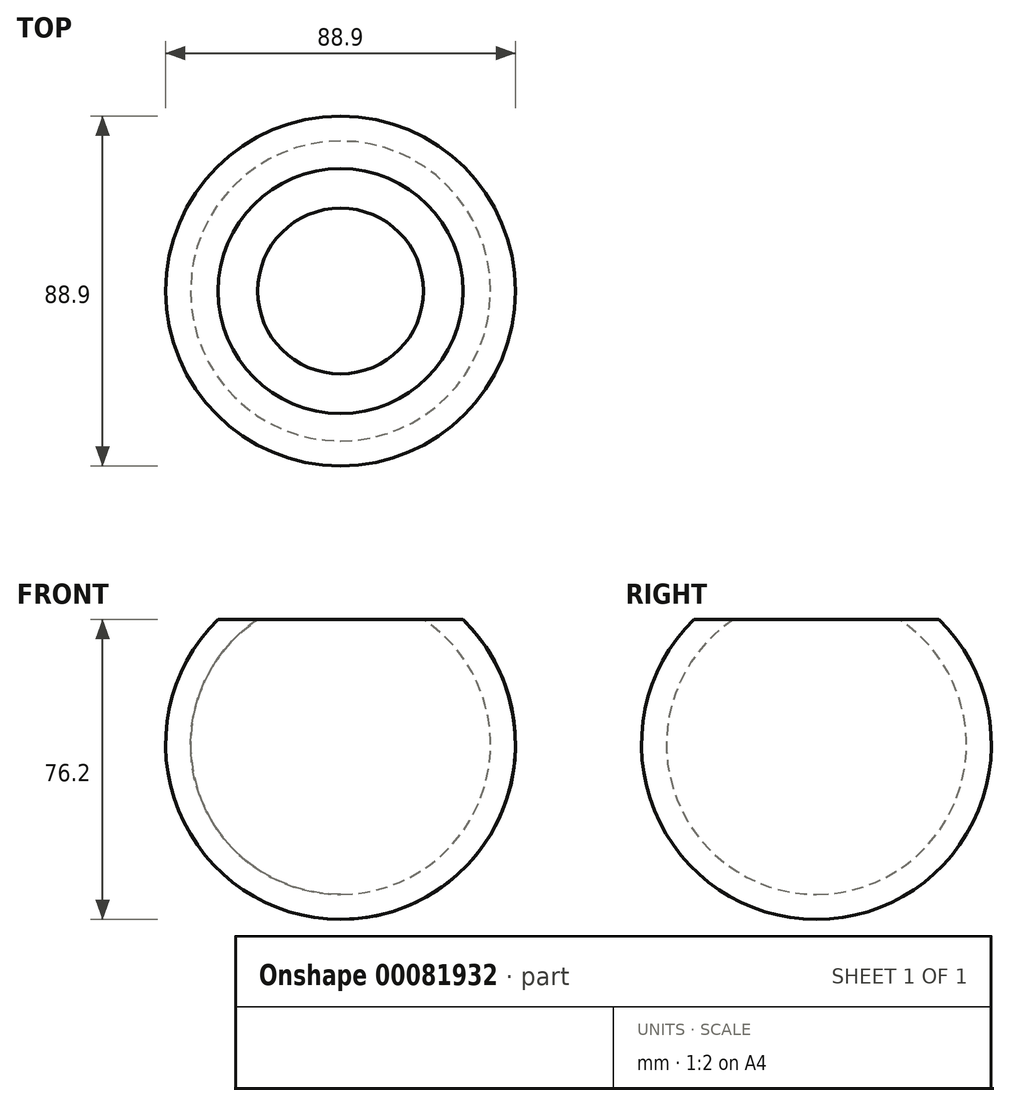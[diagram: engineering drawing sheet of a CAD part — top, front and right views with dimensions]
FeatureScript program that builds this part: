
annotation { "Feature Type Name" : "Feature", "Feature Type Description" : "" }
export const myFeature = defineFeature(function(context is Context, id is Id, definition is map)
    precondition{}
    {
        {
            var Q0;
            Q0=qCreatedBy(makeId("Front.planeOp"),FACE);
            var sketch = newSketch(context, id + "F0", { "sketchPlane" : qUnion([Q0])});
            skArc(sketch, "E0", {"start": v(0, 38.1) * mm, "mid": v(-38.1, 0) * mm, "end": v(0, -38.1) * mm});
            skArc(sketch, "E1", {"start": v(0, 44.45) * mm, "mid": v(-44.45, 0) * mm, "end": v(0, -44.45) * mm});
            skLineSegment(sketch, "E2", {"start": v(0, 44.45) * mm, "end": v(0, 38.1) * mm});
            skLineSegment(sketch, "E3", {"start": v(0, -38.1) * mm, "end": v(0, -44.45) * mm});
            skLineSegment(sketch, "E4", {"start": v(0, 38.1) * mm, "end": v(0, -38.1) * mm, "construction": true});
            skSolve(sketch);
        }
        {
            var Q0;
            Q0=makeQuery(id+"F0.imprint","IMPRINT",FACE,{"disambiguationData":[TD([[makeQuery(id+"F0.imprint","IMPRINT",EDGE,{"derivedFrom":sQuery(id+"F0.wireOp",EDGE,"E0")}),-1.0]])]});
            var Q1;
            Q1=sQuery(id+"F0.wireOp",EDGE,"E4");
            revolve(context, id + "F1", {"entities" : qUnion([Q0]), "axis" : qUnion([Q1]), "revolveType" : RevolveType.FULL});
        }
        {
            var Q0;
            Q0=qCreatedBy(makeId("Right.planeOp"),FACE);
            var sketch = newSketch(context, id + "F2", { "sketchPlane" : qUnion([Q0])});
            skLineSegment(sketch, "E5.bottom", {"start": v(-111.26, 95.93) * mm, "end": v(122.57, 95.93) * mm});
            skLineSegment(sketch, "E5.top", {"start": v(-111.26, 31.75) * mm, "end": v(122.57, 31.75) * mm});
            skLineSegment(sketch, "E5.left", {"start": v(-111.26, 95.93) * mm, "end": v(-111.26, 31.75) * mm});
            skLineSegment(sketch, "E5.right", {"start": v(122.57, 95.93) * mm, "end": v(122.57, 31.75) * mm});
            skSolve(sketch);
        }
        {
            var Q0;
            Q0=makeQuery(id+"F2.imprint","IMPRINT",FACE,{"disambiguationData":[TD([[makeQuery(id+"F2.imprint","IMPRINT",EDGE,{"derivedFrom":sQuery(id+"F2.wireOp",EDGE,"E5.bottom")}),-1.0]])]});
            extrude(context, id + "F3", {"entities" : qUnion([Q0]), "operationType" : NewBodyOperationType.REMOVE, "endBound" : BoundingType.SYMMETRIC, "depth" : 127 * mm});
        }
    });
